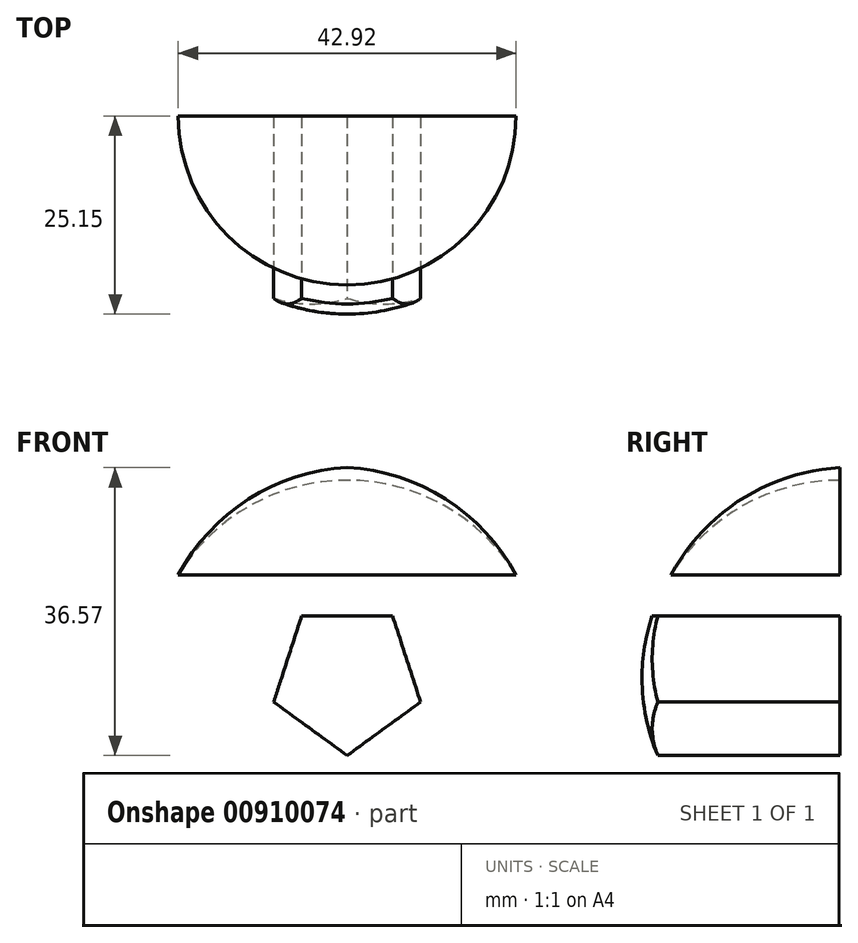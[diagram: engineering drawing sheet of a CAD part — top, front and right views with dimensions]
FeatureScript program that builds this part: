
annotation { "Feature Type Name" : "Feature", "Feature Type Description" : "" }
export const myFeature = defineFeature(function(context is Context, id is Id, definition is map)
    precondition{}
    {
        {
            var Q0;
            Q0=qCreatedBy(makeId("Front.planeOp"),FACE);
            var sketch = newSketch(context, id + "F0", { "sketchPlane" : qUnion([Q0])});
            skLineSegment(sketch, "E0", {"start": v(0, 26.76) * mm, "end": v(0, -25.12) * mm});
            skArc(sketch, "E1", {"start": v(0, -25.12) * mm, "mid": v(24.55, 0.82) * mm, "end": v(0, 26.76) * mm});
            skSolve(sketch);
        }
        {
            var Q0;
            Q0=makeQuery(id+"F0.imprint","IMPRINT",FACE,{"disambiguationData":[TD([[makeQuery(id+"F0.imprint","IMPRINT",EDGE,{"derivedFrom":sQuery(id+"F0.wireOp",EDGE,"E0")}),1.0]])]});
            var Q1;
            Q1=sQuery(id+"F0.wireOp",EDGE,"E0");
            revolve(context, id + "F1", {"surfaceOperationType" : NewSurfaceOperationType.NEW, "entities" : qUnion([Q0]), "axis" : qUnion([Q1]), "revolveType" : RevolveType.FULL});
        }
        {
            var Q0;
            Q0=qCreatedBy(makeId("Front.planeOp"),FACE);
            cPlane(context, id + "F2", {"entities" : qUnion([Q0]), "cplaneType" : CPlaneType.OFFSET, "offset" : 25.4 * mm, "width" : 152.4 * mm, "height" : 152.4 * mm});
        }
        {
            var Q0;
            Q0=qCreatedBy(id+"F2.planeOp",FACE);
            var sketch = newSketch(context, id + "F3", { "sketchPlane" : qUnion([Q0])});
            skCircle(sketch, "E2.cCircle", {"center": v(0, 0) * mm, "radius": 7.94 * mm, "construction": true});
            skLineSegment(sketch, "E2.0", {"start": v(-5.77, 7.94) * mm, "end": v(5.77, 7.94) * mm});
            skLineSegment(sketch, "E2.1", {"start": v(5.77, 7.94) * mm, "end": v(9.33, -3.03) * mm});
            skLineSegment(sketch, "E2.2", {"start": v(9.33, -3.03) * mm, "end": v(0, -9.81) * mm});
            skLineSegment(sketch, "E2.3", {"start": v(0, -9.81) * mm, "end": v(-9.33, -3.03) * mm});
            skLineSegment(sketch, "E2.4", {"start": v(-9.33, -3.03) * mm, "end": v(-5.77, 7.94) * mm});
            skPoint(sketch, "E2.0.midPoint", {"position": v(0, 7.94) * mm});
            skSolve(sketch);
        }
        {
            var Q0;
            Q0=makeQuery(id+"F3.imprint","IMPRINT",FACE,{"disambiguationData":[TD([[makeQuery(id+"F3.imprint","IMPRINT",EDGE,{"derivedFrom":sQuery(id+"F3.wireOp",EDGE,"E2.0")}),-1.0]])]});
            extrude(context, id + "F4", {"entities" : qUnion([Q0]), "oppositeDirection" : true, "depth" : 25.4 * mm, "offsetDistance" : 25.4 * mm});
        }
        {
            var Q0;
            Q0=qCreatedBy(makeId("Top.planeOp"),FACE);
            var sketch = newSketch(context, id + "F5", { "sketchPlane" : qUnion([Q0])});
            skArc(sketch, "E3", {"start": v(0, -25.15) * mm, "mid": v(17.78, -17.78) * mm, "end": v(25.15, 0) * mm});
            skLineSegment(sketch, "E4", {"start": v(25.15, 0) * mm, "end": v(0, 0) * mm});
            skLineSegment(sketch, "E5", {"start": v(0, 0) * mm, "end": v(0, -25.15) * mm, "construction": true});
            skLineSegment(sketch, "E6", {"start": v(25.15, 0) * mm, "end": v(30.68, 0) * mm});
            skLineSegment(sketch, "E7", {"start": v(30.68, 0) * mm, "end": v(30.68, -31.18) * mm});
            skLineSegment(sketch, "E8", {"start": v(30.68, -31.18) * mm, "end": v(0, -31.18) * mm});
            skLineSegment(sketch, "E9", {"start": v(0, -31.18) * mm, "end": v(0, -25.15) * mm});
            skSolve(sketch);
        }
        {
            var Q0;
            Q0=makeQuery(id+"F5.imprint","IMPRINT",FACE,{"disambiguationData":[TD([[makeQuery(id+"F5.imprint","IMPRINT",EDGE,{"derivedFrom":sQuery(id+"F5.wireOp",EDGE,"E3")}),-1.0]])]});
            var Q1;
            Q1=sQuery(id+"F5.wireOp",EDGE,"E5");
            revolve(context, id + "F6", {"operationType" : NewBodyOperationType.REMOVE, "surfaceOperationType" : NewSurfaceOperationType.NEW, "entities" : qUnion([Q0]), "axis" : qUnion([Q1]), "revolveType" : RevolveType.FULL, "oppositeDirection" : true});
        }
    });
